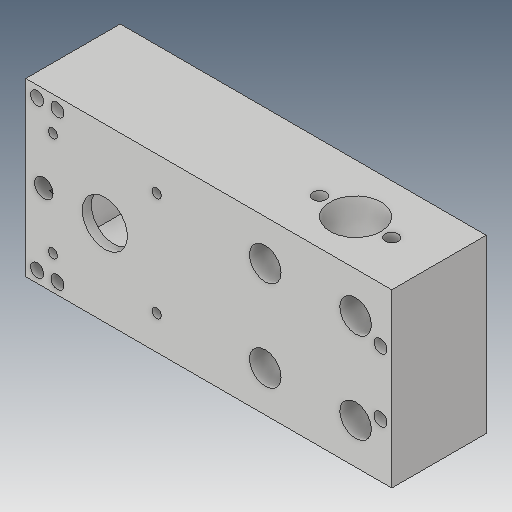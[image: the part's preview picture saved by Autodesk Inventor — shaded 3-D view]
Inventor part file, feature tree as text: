
AUTODESK INVENTOR PART (.ipt)
format: ipt  version: 2019.4 (Build 234330000, 330)  size: 283,648 bytes
history: native  units: mm
features: reference x31, other x12, sketch x7, extrude x6, plane x2, projected_geometry x2, hole x1
ambient origin geometry x8: Origin, YZ Plane, XZ Plane, XY Plane, X Axis, Y Axis, Z Axis, Center Point
bodies: Solid1 (feature_tree)
feature tree (61):
  plane  "Work Plane1"
  plane  "Work Plane2"
  extrude  "Extrusion1"  Depth=6.0mm
  extrude  "Extrusion2"  Depth=28.5mm
  extrude  "Extrusion3"  Depth=10.0mm
  hole  "Hole1"  [1 undecoded]
  extrude  "Extrusion14"  Depth=38.0mm
  extrude  "Extrusion15"  Depth=4.0mm
  extrude  "Extrusion16"  Depth=4.0mm TaperAngle=0.0deg
  sketch  "Sketch1"  dims[d0=6.0mm d1=6.0mm]
  reference  "Reference1"
  reference  "Reference2"
  reference  "Reference3"
  reference  "Reference4"
  reference  "Reference5"
  reference  "Reference6"
  reference  "Reference7"
  reference  "Reference8"
  reference  "Reference9"
  reference  "Reference10"
  reference  "Reference11"
  sketch  "Sketch2"  dims[d8=28.5mm d9=28.5mm]
  projected_geometry  "Projected Loop1"
  reference  "Reference12"
  reference  "Reference13"
  sketch  "Sketch3"  dims[d10=10.0mm d11=0.0mm d12=10.0mm]
  reference  "Reference14"
  reference  "Reference15"
  reference  "Reference16"
  sketch  "Sketch4"  dims[d13=2.0mm d14=0.0mm d15=0.5mm]
  reference  "Reference19"
  reference  "Reference20"
  sketch  "Sketch15"  dims[d16=2.0mm d17=0.0mm]
  reference  "Reference25"
  reference  "Reference26"
  sketch  "Sketch16"  dims[d18=3.5mm d19=6.0mm d20=7.0mm d21=6.0mm d22=90.0deg d23=20.0mm d24=20.594885mm d25=38.0mm]
  projected_geometry  "Projected Loop13"
  sketch  "Sketch17"  dims[d26=30.0mm d27=27.0mm d90=4.0mm d91=0.0mm d96=4.1mm d97=4.0mm d98=0.0mm d99=4.0mm d100=2.9mm d101=2.9mm d102=2.5mm d103=2.5mm d104=5.0mm d105=2.9mm d106=2.9mm d107=4.0mm d108=0.0mm d109=2.9mm d110=2.9mm d111=2.5mm d112=2.9mm d113=2.9mm d114=7.0mm d115=7.0mm]
  reference  "Reference27"
  reference  "Reference28"
  reference  "Reference29"
  reference  "Reference30"
  reference  "Reference31"
  reference  "Reference32"
  reference  "Reference33"
  reference  "Reference34"
  reference  "Reference35"
  reference  "Reference36"
  reference  "Reference37"
  other  "Assembly_Opentrons_Autofocus_v2.iam"
  other  "00_MGN12H, LINEAR GUIDE BLOCK:1"
  other  "00_NEMA11:2"
  other  "Lagerschild_11_1"
  other  "Welle_11_2"
  other  "DIN 912 - replaced by DIN EN ISO 4762 M4 x 12:1"
  other  "00_spindel_slide:1"
  other  "00_COMAR_Mirror_10mm:1"
  other  "07_OPENTRONS_Autofocus_objectivemount_v0:1"
  other  "01_Slide_camera_flexure_v1:1"
  other  "opentrons_Gearbox:1"
  other  "00_MGN12C, LINEAR GUIDE BLOCK:1"
note: 1 required parameter value undecoded (feature->parameter linkage not recoverable at this tier; creation-order binding heuristic only, values carry confidence <= 0.55)
